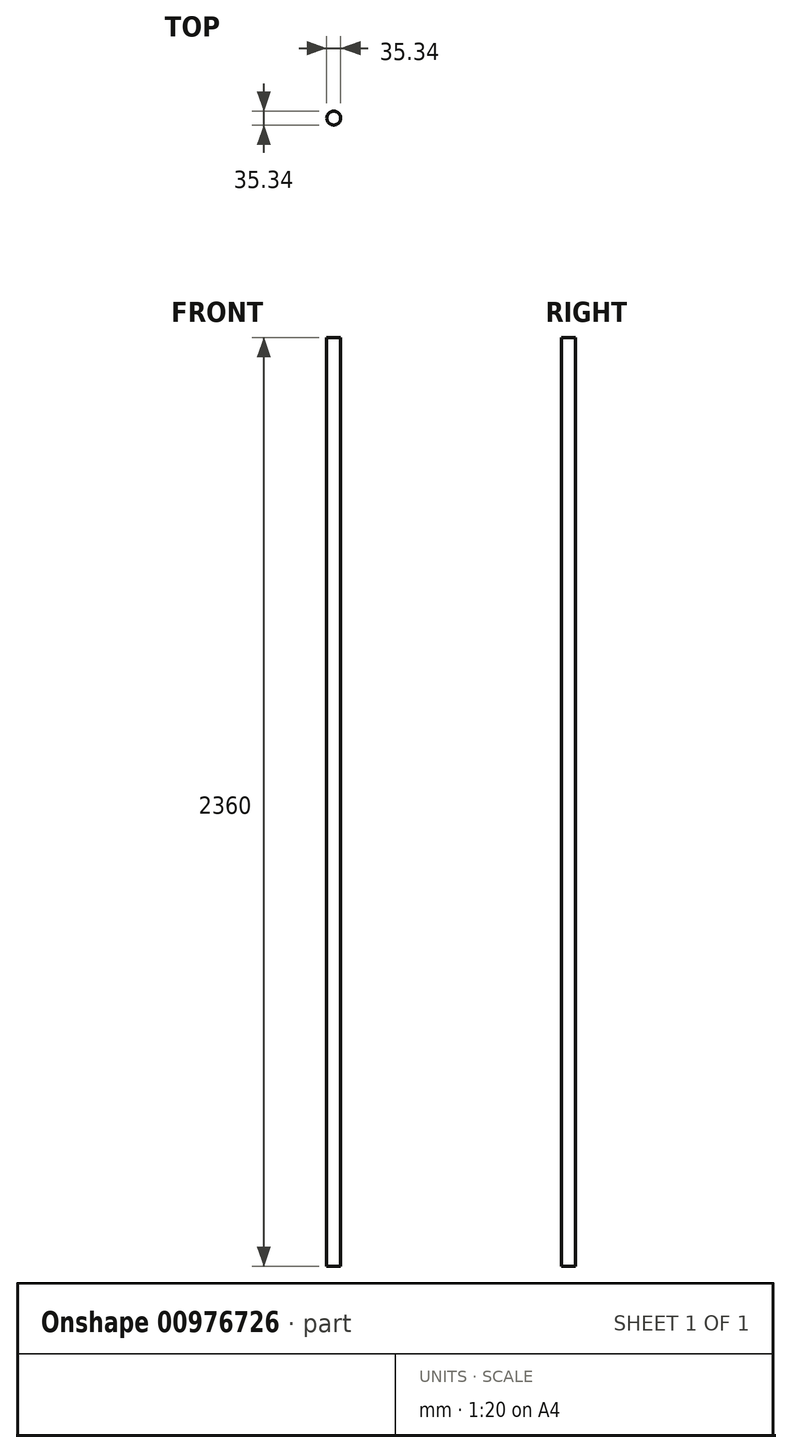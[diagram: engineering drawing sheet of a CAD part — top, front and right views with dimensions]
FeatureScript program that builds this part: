
annotation { "Feature Type Name" : "Feature", "Feature Type Description" : "" }
export const myFeature = defineFeature(function(context is Context, id is Id, definition is map)
    precondition{}
    {
        {
            var Q0;
            Q0=qCreatedBy(makeId("Top.planeOp"),FACE);
            var sketch = newSketch(context, id + "F0", { "sketchPlane" : qUnion([Q0])});
            skCircle(sketch, "E0", {"center": v(0, 0) * mm, "radius": 17.67 * mm});
            skSolve(sketch);
        }
        {
            var Q0;
            Q0=makeQuery(id+"F0.imprint","IMPRINT",FACE,{"disambiguationData":[TD([[makeQuery(id+"F0.imprint","IMPRINT",EDGE,{"derivedFrom":sQuery(id+"F0.wireOp",EDGE,"E0")}),1.0]])]});
            extrude(context, id + "F1", {"entities" : qUnion([Q0]), "depth" : 2360 * mm, "offsetDistance" : 25 * mm});
        }
    });
